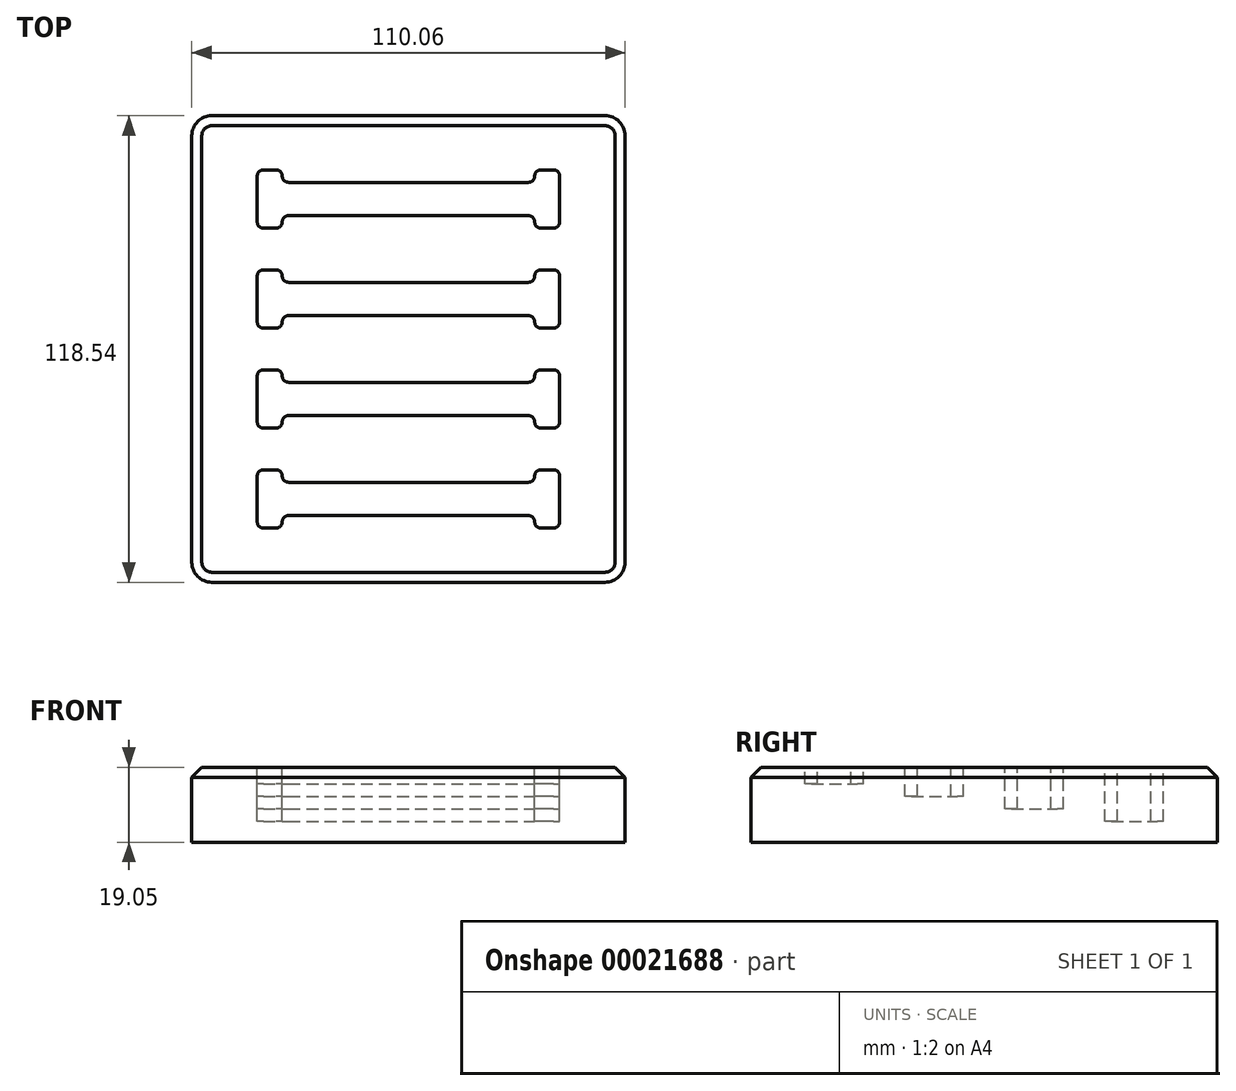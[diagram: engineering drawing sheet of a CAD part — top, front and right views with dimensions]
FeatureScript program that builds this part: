
annotation { "Feature Type Name" : "Feature", "Feature Type Description" : "" }
export const myFeature = defineFeature(function(context is Context, id is Id, definition is map)
    precondition{}
    {
        {
            var Q0;
            Q0=qCreatedBy(makeId("Top.planeOp"),FACE);
            var sketch = newSketch(context, id + "F0", { "sketchPlane" : qUnion([Q0])});
            skLineSegment(sketch, "E0.bottom", {"start": v(-55.03, 59.27) * mm, "end": v(55.03, 59.27) * mm});
            skLineSegment(sketch, "E0.top", {"start": v(-55.03, -59.27) * mm, "end": v(55.03, -59.27) * mm});
            skLineSegment(sketch, "E0.left", {"start": v(-55.03, 59.27) * mm, "end": v(-55.03, -59.27) * mm});
            skLineSegment(sketch, "E0.right", {"start": v(55.03, 59.27) * mm, "end": v(55.03, -59.27) * mm});
            skSolve(sketch);
        }
        {
            var Q0;
            Q0 = qSketchRegion(id + "F0", true);
            extrude(context, id + "F1", {"entities" : qUnion([Q0]), "depth" : 19.05 * mm});
        }
        {
            var Q0;
            Q0=makeQuery(id+"F1.opExtrude","CAP_FACE",FACE,{"disambiguationData":[OSD([sQuery(id+"F0.wireOp",EDGE,"E0.bottom"),sQuery(id+"F0.wireOp",EDGE,"E0.top"),sQuery(id+"F0.wireOp",EDGE,"E0.left"),sQuery(id+"F0.wireOp",EDGE,"E0.right")])],"isStart":false});
            var sketch = newSketch(context, id + "F2", { "sketchPlane" : qUnion([Q0])});
            skLineSegment(sketch, "E1.left", {"start": v(-38.42, 38.1) * mm, "end": v(-38.42, 33.87) * mm});
            skLineSegment(sketch, "E2", {"start": v(-38.42, 33.87) * mm, "end": v(-38.42, 30.7) * mm});
            skLineSegment(sketch, "E3", {"start": v(-38.42, 30.7) * mm, "end": v(-32.07, 30.7) * mm});
            skLineSegment(sketch, "E4", {"start": v(-32.07, 30.7) * mm, "end": v(-32.07, 33.87) * mm});
            skLineSegment(sketch, "E5", {"start": v(-32.07, 33.87) * mm, "end": v(0, 33.87) * mm});
            skLineSegment(sketch, "E6", {"start": v(-38.42, 38.1) * mm, "end": v(0, 38.1) * mm, "construction": true});
            skLineSegment(sketch, "E7.MirrorCS", {"start": v(-32.07, 42.33) * mm, "end": v(0, 42.33) * mm});
            skLineSegment(sketch, "E8.MirrorCS", {"start": v(-32.07, 45.5) * mm, "end": v(-32.07, 42.33) * mm});
            skLineSegment(sketch, "E9.MirrorCS", {"start": v(-38.42, 45.5) * mm, "end": v(-32.07, 45.5) * mm});
            skLineSegment(sketch, "E10.MirrorCS", {"start": v(-38.42, 38.1) * mm, "end": v(-38.42, 42.33) * mm});
            skLineSegment(sketch, "E11.MirrorCS", {"start": v(-38.42, 42.33) * mm, "end": v(-38.42, 45.5) * mm});
            skLineSegment(sketch, "E12", {"start": v(0, 33.87) * mm, "end": v(0, 42.33) * mm, "construction": true});
            skLineSegment(sketch, "E13.MirrorCS", {"start": v(32.07, 42.33) * mm, "end": v(0, 42.33) * mm});
            skLineSegment(sketch, "E14.MirrorCS", {"start": v(32.07, 45.5) * mm, "end": v(32.07, 42.33) * mm});
            skLineSegment(sketch, "E15.MirrorCS", {"start": v(38.42, 45.5) * mm, "end": v(32.07, 45.5) * mm});
            skLineSegment(sketch, "E16.MirrorCS", {"start": v(38.42, 42.33) * mm, "end": v(38.42, 45.5) * mm});
            skLineSegment(sketch, "E17.MirrorCS", {"start": v(38.42, 38.1) * mm, "end": v(38.42, 42.33) * mm});
            skLineSegment(sketch, "E18.MirrorCS", {"start": v(38.42, 38.1) * mm, "end": v(38.42, 33.87) * mm});
            skLineSegment(sketch, "E19.MirrorCS", {"start": v(38.42, 33.87) * mm, "end": v(38.42, 30.7) * mm});
            skLineSegment(sketch, "E20.MirrorCS", {"start": v(38.42, 30.7) * mm, "end": v(32.07, 30.7) * mm});
            skLineSegment(sketch, "E21.MirrorCS", {"start": v(32.07, 33.87) * mm, "end": v(0, 33.87) * mm});
            skLineSegment(sketch, "E22.MirrorCS", {"start": v(32.07, 30.7) * mm, "end": v(32.07, 33.87) * mm});
            skSolve(sketch);
        }
        {
            var Q0;
            Q0 = qSketchRegion(id + "F2", true);
            extrude(context, id + "F3", {"entities" : qUnion([Q0]), "operationType" : NewBodyOperationType.REMOVE, "oppositeDirection" : true, "depth" : 13.76 * mm});
        }
        {
            var Q0;
            Q0=makeQuery(id+"F1.opExtrude","CAP_FACE",FACE,{"disambiguationData":[OSD([sQuery(id+"F0.wireOp",EDGE,"E0.bottom"),sQuery(id+"F0.wireOp",EDGE,"E0.top"),sQuery(id+"F0.wireOp",EDGE,"E0.left"),sQuery(id+"F0.wireOp",EDGE,"E0.right")])],"isStart":false});
            var sketch = newSketch(context, id + "F4", { "sketchPlane" : qUnion([Q0])});
            skLineSegment(sketch, "E23.left", {"start": v(-38.42, 12.7) * mm, "end": v(-38.42, 8.47) * mm});
            skLineSegment(sketch, "E24", {"start": v(-38.42, 8.47) * mm, "end": v(-38.42, 5.3) * mm});
            skLineSegment(sketch, "E25", {"start": v(-38.42, 5.3) * mm, "end": v(-32.07, 5.3) * mm});
            skLineSegment(sketch, "E26", {"start": v(-32.07, 5.3) * mm, "end": v(-32.07, 8.47) * mm});
            skLineSegment(sketch, "E27", {"start": v(-32.07, 8.47) * mm, "end": v(0, 8.47) * mm});
            skLineSegment(sketch, "E28", {"start": v(-38.42, 12.7) * mm, "end": v(3.73, 12.7) * mm, "construction": true});
            skLineSegment(sketch, "E29.MirrorCS", {"start": v(-32.07, 16.93) * mm, "end": v(0, 16.93) * mm});
            skLineSegment(sketch, "E30.MirrorCS", {"start": v(-32.07, 20.1) * mm, "end": v(-32.07, 16.93) * mm});
            skLineSegment(sketch, "E31.MirrorCS", {"start": v(-38.42, 20.1) * mm, "end": v(-32.07, 20.1) * mm});
            skLineSegment(sketch, "E32.MirrorCS", {"start": v(-38.42, 12.7) * mm, "end": v(-38.42, 16.93) * mm});
            skLineSegment(sketch, "E33.MirrorCS", {"start": v(-38.42, 16.93) * mm, "end": v(-38.42, 20.1) * mm});
            skLineSegment(sketch, "E34", {"start": v(0, 8.47) * mm, "end": v(0, 16.93) * mm, "construction": true});
            skLineSegment(sketch, "E35.MirrorCS", {"start": v(32.07, 16.93) * mm, "end": v(0, 16.93) * mm});
            skLineSegment(sketch, "E36.MirrorCS", {"start": v(32.07, 20.1) * mm, "end": v(32.07, 16.93) * mm});
            skLineSegment(sketch, "E37.MirrorCS", {"start": v(38.42, 20.1) * mm, "end": v(32.07, 20.1) * mm});
            skLineSegment(sketch, "E38.MirrorCS", {"start": v(38.42, 16.93) * mm, "end": v(38.42, 20.1) * mm});
            skLineSegment(sketch, "E39.MirrorCS", {"start": v(38.42, 12.7) * mm, "end": v(38.42, 16.93) * mm});
            skLineSegment(sketch, "E40.MirrorCS", {"start": v(38.42, 12.7) * mm, "end": v(38.42, 8.47) * mm});
            skLineSegment(sketch, "E41.MirrorCS", {"start": v(38.42, 8.47) * mm, "end": v(38.42, 5.3) * mm});
            skLineSegment(sketch, "E42.MirrorCS", {"start": v(38.42, 5.3) * mm, "end": v(32.07, 5.3) * mm});
            skLineSegment(sketch, "E43.MirrorCS", {"start": v(32.07, 8.47) * mm, "end": v(0, 8.47) * mm});
            skLineSegment(sketch, "E44.MirrorCS", {"start": v(32.07, 5.3) * mm, "end": v(32.07, 8.47) * mm});
            skSolve(sketch);
        }
        {
            var Q0;
            Q0 = qSketchRegion(id + "F4", true);
            extrude(context, id + "F5", {"entities" : qUnion([Q0]), "operationType" : NewBodyOperationType.REMOVE, "oppositeDirection" : true, "depth" : 10.58 * mm});
        }
        {
            var Q0;
            Q0=makeQuery(id+"F1.opExtrude","CAP_FACE",FACE,{"disambiguationData":[OSD([sQuery(id+"F0.wireOp",EDGE,"E0.bottom"),sQuery(id+"F0.wireOp",EDGE,"E0.top"),sQuery(id+"F0.wireOp",EDGE,"E0.left"),sQuery(id+"F0.wireOp",EDGE,"E0.right")])],"isStart":false});
            var sketch = newSketch(context, id + "F6", { "sketchPlane" : qUnion([Q0])});
            skLineSegment(sketch, "E45.left", {"start": v(-38.42, -12.7) * mm, "end": v(-38.42, -16.93) * mm});
            skLineSegment(sketch, "E46", {"start": v(-38.42, -16.93) * mm, "end": v(-38.42, -20.1) * mm});
            skLineSegment(sketch, "E47", {"start": v(-38.42, -20.1) * mm, "end": v(-32.07, -20.1) * mm});
            skLineSegment(sketch, "E48", {"start": v(-32.07, -20.1) * mm, "end": v(-32.07, -16.93) * mm});
            skLineSegment(sketch, "E49", {"start": v(-32.07, -16.93) * mm, "end": v(0, -16.93) * mm});
            skLineSegment(sketch, "E50", {"start": v(-38.42, -12.7) * mm, "end": v(-19.4, -12.7) * mm, "construction": true});
            skLineSegment(sketch, "E51.MirrorCS", {"start": v(-32.07, -8.47) * mm, "end": v(0, -8.47) * mm});
            skLineSegment(sketch, "E52.MirrorCS", {"start": v(-32.07, -5.3) * mm, "end": v(-32.07, -8.47) * mm});
            skLineSegment(sketch, "E53.MirrorCS", {"start": v(-38.42, -5.3) * mm, "end": v(-32.07, -5.3) * mm});
            skLineSegment(sketch, "E54.MirrorCS", {"start": v(-38.42, -12.7) * mm, "end": v(-38.42, -8.47) * mm});
            skLineSegment(sketch, "E55.MirrorCS", {"start": v(-38.42, -8.47) * mm, "end": v(-38.42, -5.3) * mm});
            skLineSegment(sketch, "E56", {"start": v(0, -16.93) * mm, "end": v(0, -8.47) * mm, "construction": true});
            skLineSegment(sketch, "E57.MirrorCS", {"start": v(32.07, -8.47) * mm, "end": v(0, -8.47) * mm});
            skLineSegment(sketch, "E58.MirrorCS", {"start": v(32.07, -5.3) * mm, "end": v(32.07, -8.47) * mm});
            skLineSegment(sketch, "E59.MirrorCS", {"start": v(38.42, -5.3) * mm, "end": v(32.07, -5.3) * mm});
            skLineSegment(sketch, "E60.MirrorCS", {"start": v(38.42, -8.47) * mm, "end": v(38.42, -5.3) * mm});
            skLineSegment(sketch, "E61.MirrorCS", {"start": v(38.42, -12.7) * mm, "end": v(38.42, -8.47) * mm});
            skLineSegment(sketch, "E62.MirrorCS", {"start": v(38.42, -12.7) * mm, "end": v(38.42, -16.93) * mm});
            skLineSegment(sketch, "E63.MirrorCS", {"start": v(38.42, -16.93) * mm, "end": v(38.42, -20.1) * mm});
            skLineSegment(sketch, "E64.MirrorCS", {"start": v(38.42, -20.1) * mm, "end": v(32.07, -20.1) * mm});
            skLineSegment(sketch, "E65.MirrorCS", {"start": v(32.07, -16.93) * mm, "end": v(0, -16.93) * mm});
            skLineSegment(sketch, "E66.MirrorCS", {"start": v(32.07, -20.1) * mm, "end": v(32.07, -16.93) * mm});
            skSolve(sketch);
        }
        {
            var Q0;
            Q0 = qSketchRegion(id + "F6", true);
            extrude(context, id + "F7", {"entities" : qUnion([Q0]), "operationType" : NewBodyOperationType.REMOVE, "oppositeDirection" : true, "depth" : 7.4 * mm});
        }
        {
            var Q0;
            Q0=makeQuery(id+"F1.opExtrude","CAP_FACE",FACE,{"disambiguationData":[OSD([sQuery(id+"F0.wireOp",EDGE,"E0.bottom"),sQuery(id+"F0.wireOp",EDGE,"E0.top"),sQuery(id+"F0.wireOp",EDGE,"E0.left"),sQuery(id+"F0.wireOp",EDGE,"E0.right")])],"isStart":false});
            var sketch = newSketch(context, id + "F8", { "sketchPlane" : qUnion([Q0])});
            skLineSegment(sketch, "E67.left", {"start": v(-38.42, -38.1) * mm, "end": v(-38.42, -42.33) * mm});
            skLineSegment(sketch, "E68", {"start": v(-38.42, -42.33) * mm, "end": v(-38.42, -45.5) * mm});
            skLineSegment(sketch, "E69", {"start": v(-38.42, -45.5) * mm, "end": v(-32.07, -45.5) * mm});
            skLineSegment(sketch, "E70", {"start": v(-32.07, -45.5) * mm, "end": v(-32.07, -42.33) * mm});
            skLineSegment(sketch, "E71", {"start": v(-32.07, -42.33) * mm, "end": v(0, -42.33) * mm});
            skLineSegment(sketch, "E72", {"start": v(-38.42, -38.1) * mm, "end": v(-1.73, -38.1) * mm, "construction": true});
            skLineSegment(sketch, "E73.MirrorCS", {"start": v(-32.07, -33.87) * mm, "end": v(0, -33.87) * mm});
            skLineSegment(sketch, "E74.MirrorCS", {"start": v(-32.07, -30.7) * mm, "end": v(-32.07, -33.87) * mm});
            skLineSegment(sketch, "E75.MirrorCS", {"start": v(-38.42, -30.7) * mm, "end": v(-32.07, -30.7) * mm});
            skLineSegment(sketch, "E76.MirrorCS", {"start": v(-38.42, -38.1) * mm, "end": v(-38.42, -33.87) * mm});
            skLineSegment(sketch, "E77.MirrorCS", {"start": v(-38.42, -33.87) * mm, "end": v(-38.42, -30.7) * mm});
            skLineSegment(sketch, "E78", {"start": v(0, -42.33) * mm, "end": v(0, -33.87) * mm, "construction": true});
            skLineSegment(sketch, "E79.MirrorCS", {"start": v(32.07, -33.87) * mm, "end": v(0, -33.87) * mm});
            skLineSegment(sketch, "E80.MirrorCS", {"start": v(32.07, -30.7) * mm, "end": v(32.07, -33.87) * mm});
            skLineSegment(sketch, "E81.MirrorCS", {"start": v(38.42, -30.7) * mm, "end": v(32.07, -30.7) * mm});
            skLineSegment(sketch, "E82.MirrorCS", {"start": v(38.42, -33.87) * mm, "end": v(38.42, -30.7) * mm});
            skLineSegment(sketch, "E83.MirrorCS", {"start": v(38.42, -38.1) * mm, "end": v(38.42, -33.87) * mm});
            skLineSegment(sketch, "E84.MirrorCS", {"start": v(38.42, -38.1) * mm, "end": v(38.42, -42.33) * mm});
            skLineSegment(sketch, "E85.MirrorCS", {"start": v(38.42, -42.33) * mm, "end": v(38.42, -45.5) * mm});
            skLineSegment(sketch, "E86.MirrorCS", {"start": v(38.42, -45.5) * mm, "end": v(32.07, -45.5) * mm});
            skLineSegment(sketch, "E87.MirrorCS", {"start": v(32.07, -42.33) * mm, "end": v(0, -42.33) * mm});
            skLineSegment(sketch, "E88.MirrorCS", {"start": v(32.07, -45.5) * mm, "end": v(32.07, -42.33) * mm});
            skSolve(sketch);
        }
        {
            var Q0;
            Q0 = qSketchRegion(id + "F8", true);
            extrude(context, id + "F9", {"entities" : qUnion([Q0]), "operationType" : NewBodyOperationType.REMOVE, "oppositeDirection" : true, "depth" : 4.23 * mm});
        }
        {
            var Q0;
            Q0=makeQuery(id+"F9.boolean.opBoolean","COPY",EDGE,{"derivedFrom":makeQuery(id+"F9.opExtrude","SWEPT_EDGE",EDGE,{"disambiguationData":[OSD([sQuery(id+"F8.wireOp",EDGE,"E75.MirrorCS"),sQuery(id+"F8.wireOp",EDGE,"E77.MirrorCS")])]})});
            var Q1;
            Q1=makeQuery(id+"F7.boolean.opBoolean","COPY",EDGE,{"derivedFrom":makeQuery(id+"F7.opExtrude","SWEPT_EDGE",EDGE,{"disambiguationData":[OSD([sQuery(id+"F6.wireOp",EDGE,"E53.MirrorCS"),sQuery(id+"F6.wireOp",EDGE,"E55.MirrorCS")])]})});
            var Q2;
            Q2=makeQuery(id+"F5.boolean.opBoolean","COPY",EDGE,{"derivedFrom":makeQuery(id+"F5.opExtrude","SWEPT_EDGE",EDGE,{"disambiguationData":[OSD([sQuery(id+"F4.wireOp",EDGE,"E31.MirrorCS"),sQuery(id+"F4.wireOp",EDGE,"E33.MirrorCS")])]})});
            var Q3;
            Q3=makeQuery(id+"F3.boolean.opBoolean","COPY",EDGE,{"derivedFrom":makeQuery(id+"F3.opExtrude","SWEPT_EDGE",EDGE,{"disambiguationData":[OSD([sQuery(id+"F2.wireOp",EDGE,"E9.MirrorCS"),sQuery(id+"F2.wireOp",EDGE,"E11.MirrorCS")])]})});
            var Q4;
            Q4=makeQuery(id+"F3.boolean.opBoolean","COPY",EDGE,{"derivedFrom":makeQuery(id+"F3.opExtrude","SWEPT_EDGE",EDGE,{"disambiguationData":[OSD([sQuery(id+"F2.wireOp",EDGE,"E7.MirrorCS"),sQuery(id+"F2.wireOp",EDGE,"E8.MirrorCS")])]})});
            var Q5;
            Q5=makeQuery(id+"F5.boolean.opBoolean","COPY",EDGE,{"derivedFrom":makeQuery(id+"F5.opExtrude","SWEPT_EDGE",EDGE,{"disambiguationData":[OSD([sQuery(id+"F4.wireOp",EDGE,"E29.MirrorCS"),sQuery(id+"F4.wireOp",EDGE,"E30.MirrorCS")])]})});
            var Q6;
            Q6=makeQuery(id+"F7.boolean.opBoolean","COPY",EDGE,{"derivedFrom":makeQuery(id+"F7.opExtrude","SWEPT_EDGE",EDGE,{"disambiguationData":[OSD([sQuery(id+"F6.wireOp",EDGE,"E51.MirrorCS"),sQuery(id+"F6.wireOp",EDGE,"E52.MirrorCS")])]})});
            var Q7;
            Q7=makeQuery(id+"F9.boolean.opBoolean","COPY",EDGE,{"derivedFrom":makeQuery(id+"F9.opExtrude","SWEPT_EDGE",EDGE,{"disambiguationData":[OSD([sQuery(id+"F8.wireOp",EDGE,"E73.MirrorCS"),sQuery(id+"F8.wireOp",EDGE,"E74.MirrorCS")])]})});
            var Q8;
            Q8=makeQuery(id+"F9.boolean.opBoolean","COPY",EDGE,{"derivedFrom":makeQuery(id+"F9.opExtrude","SWEPT_EDGE",EDGE,{"disambiguationData":[OSD([sQuery(id+"F8.wireOp",EDGE,"E68"),sQuery(id+"F8.wireOp",EDGE,"E69")])]})});
            var Q9;
            Q9=makeQuery(id+"F9.boolean.opBoolean","COPY",EDGE,{"derivedFrom":makeQuery(id+"F9.opExtrude","SWEPT_EDGE",EDGE,{"disambiguationData":[OSD([sQuery(id+"F8.wireOp",EDGE,"E70"),sQuery(id+"F8.wireOp",EDGE,"E71")])]})});
            var Q10;
            Q10=makeQuery(id+"F7.boolean.opBoolean","COPY",EDGE,{"derivedFrom":makeQuery(id+"F7.opExtrude","SWEPT_EDGE",EDGE,{"disambiguationData":[OSD([sQuery(id+"F6.wireOp",EDGE,"E46"),sQuery(id+"F6.wireOp",EDGE,"E47")])]})});
            var Q11;
            Q11=makeQuery(id+"F7.boolean.opBoolean","COPY",EDGE,{"derivedFrom":makeQuery(id+"F7.opExtrude","SWEPT_EDGE",EDGE,{"disambiguationData":[OSD([sQuery(id+"F6.wireOp",EDGE,"E48"),sQuery(id+"F6.wireOp",EDGE,"E49")])]})});
            var Q12;
            Q12=makeQuery(id+"F5.boolean.opBoolean","COPY",EDGE,{"derivedFrom":makeQuery(id+"F5.opExtrude","SWEPT_EDGE",EDGE,{"disambiguationData":[OSD([sQuery(id+"F4.wireOp",EDGE,"E26"),sQuery(id+"F4.wireOp",EDGE,"E27")])]})});
            var Q13;
            Q13=makeQuery(id+"F5.boolean.opBoolean","COPY",EDGE,{"derivedFrom":makeQuery(id+"F5.opExtrude","SWEPT_EDGE",EDGE,{"disambiguationData":[OSD([sQuery(id+"F4.wireOp",EDGE,"E24"),sQuery(id+"F4.wireOp",EDGE,"E25")])]})});
            var Q14;
            Q14=makeQuery(id+"F3.boolean.opBoolean","COPY",EDGE,{"derivedFrom":makeQuery(id+"F3.opExtrude","SWEPT_EDGE",EDGE,{"disambiguationData":[OSD([sQuery(id+"F2.wireOp",EDGE,"E4"),sQuery(id+"F2.wireOp",EDGE,"E5")])]})});
            var Q15;
            Q15=makeQuery(id+"F3.boolean.opBoolean","COPY",EDGE,{"derivedFrom":makeQuery(id+"F3.opExtrude","SWEPT_EDGE",EDGE,{"disambiguationData":[OSD([sQuery(id+"F2.wireOp",EDGE,"E2"),sQuery(id+"F2.wireOp",EDGE,"E3")])]})});
            var Q16;
            Q16=makeQuery(id+"F9.boolean.opBoolean","COPY",EDGE,{"derivedFrom":makeQuery(id+"F9.opExtrude","SWEPT_EDGE",EDGE,{"disambiguationData":[OSD([sQuery(id+"F8.wireOp",EDGE,"E86.MirrorCS"),sQuery(id+"F8.wireOp",EDGE,"E88.MirrorCS")])]})});
            var Q17;
            Q17=makeQuery(id+"F9.boolean.opBoolean","COPY",EDGE,{"derivedFrom":makeQuery(id+"F9.opExtrude","SWEPT_EDGE",EDGE,{"disambiguationData":[OSD([sQuery(id+"F8.wireOp",EDGE,"E87.MirrorCS"),sQuery(id+"F8.wireOp",EDGE,"E88.MirrorCS")])]})});
            var Q18;
            Q18=makeQuery(id+"F9.boolean.opBoolean","COPY",EDGE,{"derivedFrom":makeQuery(id+"F9.opExtrude","SWEPT_EDGE",EDGE,{"disambiguationData":[OSD([sQuery(id+"F8.wireOp",EDGE,"E79.MirrorCS"),sQuery(id+"F8.wireOp",EDGE,"E80.MirrorCS")])]})});
            var Q19;
            Q19=makeQuery(id+"F7.boolean.opBoolean","COPY",EDGE,{"derivedFrom":makeQuery(id+"F7.opExtrude","SWEPT_EDGE",EDGE,{"disambiguationData":[OSD([sQuery(id+"F6.wireOp",EDGE,"E64.MirrorCS"),sQuery(id+"F6.wireOp",EDGE,"E66.MirrorCS")])]})});
            var Q20;
            Q20=makeQuery(id+"F7.boolean.opBoolean","COPY",EDGE,{"derivedFrom":makeQuery(id+"F7.opExtrude","SWEPT_EDGE",EDGE,{"disambiguationData":[OSD([sQuery(id+"F6.wireOp",EDGE,"E65.MirrorCS"),sQuery(id+"F6.wireOp",EDGE,"E66.MirrorCS")])]})});
            var Q21;
            Q21=makeQuery(id+"F7.boolean.opBoolean","COPY",EDGE,{"derivedFrom":makeQuery(id+"F7.opExtrude","SWEPT_EDGE",EDGE,{"disambiguationData":[OSD([sQuery(id+"F6.wireOp",EDGE,"E57.MirrorCS"),sQuery(id+"F6.wireOp",EDGE,"E58.MirrorCS")])]})});
            var Q22;
            Q22=makeQuery(id+"F5.boolean.opBoolean","COPY",EDGE,{"derivedFrom":makeQuery(id+"F5.opExtrude","SWEPT_EDGE",EDGE,{"disambiguationData":[OSD([sQuery(id+"F4.wireOp",EDGE,"E42.MirrorCS"),sQuery(id+"F4.wireOp",EDGE,"E44.MirrorCS")])]})});
            var Q23;
            Q23=makeQuery(id+"F5.boolean.opBoolean","COPY",EDGE,{"derivedFrom":makeQuery(id+"F5.opExtrude","SWEPT_EDGE",EDGE,{"disambiguationData":[OSD([sQuery(id+"F4.wireOp",EDGE,"E43.MirrorCS"),sQuery(id+"F4.wireOp",EDGE,"E44.MirrorCS")])]})});
            var Q24;
            Q24=makeQuery(id+"F5.boolean.opBoolean","COPY",EDGE,{"derivedFrom":makeQuery(id+"F5.opExtrude","SWEPT_EDGE",EDGE,{"disambiguationData":[OSD([sQuery(id+"F4.wireOp",EDGE,"E35.MirrorCS"),sQuery(id+"F4.wireOp",EDGE,"E36.MirrorCS")])]})});
            var Q25;
            Q25=makeQuery(id+"F3.boolean.opBoolean","COPY",EDGE,{"derivedFrom":makeQuery(id+"F3.opExtrude","SWEPT_EDGE",EDGE,{"disambiguationData":[OSD([sQuery(id+"F2.wireOp",EDGE,"E20.MirrorCS"),sQuery(id+"F2.wireOp",EDGE,"E22.MirrorCS")])]})});
            var Q26;
            Q26=makeQuery(id+"F3.boolean.opBoolean","COPY",EDGE,{"derivedFrom":makeQuery(id+"F3.opExtrude","SWEPT_EDGE",EDGE,{"disambiguationData":[OSD([sQuery(id+"F2.wireOp",EDGE,"E21.MirrorCS"),sQuery(id+"F2.wireOp",EDGE,"E22.MirrorCS")])]})});
            var Q27;
            Q27=makeQuery(id+"F3.boolean.opBoolean","COPY",EDGE,{"derivedFrom":makeQuery(id+"F3.opExtrude","SWEPT_EDGE",EDGE,{"disambiguationData":[OSD([sQuery(id+"F2.wireOp",EDGE,"E13.MirrorCS"),sQuery(id+"F2.wireOp",EDGE,"E14.MirrorCS")])]})});
            var Q28;
            Q28=makeQuery(id+"F3.boolean.opBoolean","COPY",EDGE,{"derivedFrom":makeQuery(id+"F3.opExtrude","SWEPT_EDGE",EDGE,{"disambiguationData":[OSD([sQuery(id+"F2.wireOp",EDGE,"E19.MirrorCS"),sQuery(id+"F2.wireOp",EDGE,"E20.MirrorCS")])]})});
            var Q29;
            Q29=makeQuery(id+"F5.boolean.opBoolean","COPY",EDGE,{"derivedFrom":makeQuery(id+"F5.opExtrude","SWEPT_EDGE",EDGE,{"disambiguationData":[OSD([sQuery(id+"F4.wireOp",EDGE,"E41.MirrorCS"),sQuery(id+"F4.wireOp",EDGE,"E42.MirrorCS")])]})});
            var Q30;
            Q30=makeQuery(id+"F7.boolean.opBoolean","COPY",EDGE,{"derivedFrom":makeQuery(id+"F7.opExtrude","SWEPT_EDGE",EDGE,{"disambiguationData":[OSD([sQuery(id+"F6.wireOp",EDGE,"E63.MirrorCS"),sQuery(id+"F6.wireOp",EDGE,"E64.MirrorCS")])]})});
            var Q31;
            Q31=makeQuery(id+"F9.boolean.opBoolean","COPY",EDGE,{"derivedFrom":makeQuery(id+"F9.opExtrude","SWEPT_EDGE",EDGE,{"disambiguationData":[OSD([sQuery(id+"F8.wireOp",EDGE,"E85.MirrorCS"),sQuery(id+"F8.wireOp",EDGE,"E86.MirrorCS")])]})});
            var Q32;
            Q32=makeQuery(id+"F3.boolean.opBoolean","COPY",EDGE,{"derivedFrom":makeQuery(id+"F3.opExtrude","SWEPT_EDGE",EDGE,{"disambiguationData":[OSD([sQuery(id+"F2.wireOp",EDGE,"E15.MirrorCS"),sQuery(id+"F2.wireOp",EDGE,"E16.MirrorCS")])]})});
            var Q33;
            Q33=makeQuery(id+"F5.boolean.opBoolean","COPY",EDGE,{"derivedFrom":makeQuery(id+"F5.opExtrude","SWEPT_EDGE",EDGE,{"disambiguationData":[OSD([sQuery(id+"F4.wireOp",EDGE,"E37.MirrorCS"),sQuery(id+"F4.wireOp",EDGE,"E38.MirrorCS")])]})});
            var Q34;
            Q34=makeQuery(id+"F7.boolean.opBoolean","COPY",EDGE,{"derivedFrom":makeQuery(id+"F7.opExtrude","SWEPT_EDGE",EDGE,{"disambiguationData":[OSD([sQuery(id+"F6.wireOp",EDGE,"E59.MirrorCS"),sQuery(id+"F6.wireOp",EDGE,"E60.MirrorCS")])]})});
            var Q35;
            Q35=makeQuery(id+"F9.boolean.opBoolean","COPY",EDGE,{"derivedFrom":makeQuery(id+"F9.opExtrude","SWEPT_EDGE",EDGE,{"disambiguationData":[OSD([sQuery(id+"F8.wireOp",EDGE,"E81.MirrorCS"),sQuery(id+"F8.wireOp",EDGE,"E82.MirrorCS")])]})});
            var Q36;
            Q36=makeQuery(id+"F3.boolean.opBoolean","COPY",EDGE,{"derivedFrom":makeQuery(id+"F3.opExtrude","SWEPT_EDGE",EDGE,{"disambiguationData":[OSD([sQuery(id+"F2.wireOp",EDGE,"E8.MirrorCS"),sQuery(id+"F2.wireOp",EDGE,"E9.MirrorCS")])]})});
            var Q37;
            Q37=makeQuery(id+"F5.boolean.opBoolean","COPY",EDGE,{"derivedFrom":makeQuery(id+"F5.opExtrude","SWEPT_EDGE",EDGE,{"disambiguationData":[OSD([sQuery(id+"F4.wireOp",EDGE,"E30.MirrorCS"),sQuery(id+"F4.wireOp",EDGE,"E31.MirrorCS")])]})});
            var Q38;
            Q38=makeQuery(id+"F7.boolean.opBoolean","COPY",EDGE,{"derivedFrom":makeQuery(id+"F7.opExtrude","SWEPT_EDGE",EDGE,{"disambiguationData":[OSD([sQuery(id+"F6.wireOp",EDGE,"E52.MirrorCS"),sQuery(id+"F6.wireOp",EDGE,"E53.MirrorCS")])]})});
            var Q39;
            Q39=makeQuery(id+"F9.boolean.opBoolean","COPY",EDGE,{"derivedFrom":makeQuery(id+"F9.opExtrude","SWEPT_EDGE",EDGE,{"disambiguationData":[OSD([sQuery(id+"F8.wireOp",EDGE,"E74.MirrorCS"),sQuery(id+"F8.wireOp",EDGE,"E75.MirrorCS")])]})});
            var Q40;
            Q40=makeQuery(id+"F9.boolean.opBoolean","COPY",EDGE,{"derivedFrom":makeQuery(id+"F9.opExtrude","SWEPT_EDGE",EDGE,{"disambiguationData":[OSD([sQuery(id+"F8.wireOp",EDGE,"E69"),sQuery(id+"F8.wireOp",EDGE,"E70")])]})});
            var Q41;
            Q41=makeQuery(id+"F7.boolean.opBoolean","COPY",EDGE,{"derivedFrom":makeQuery(id+"F7.opExtrude","SWEPT_EDGE",EDGE,{"disambiguationData":[OSD([sQuery(id+"F6.wireOp",EDGE,"E47"),sQuery(id+"F6.wireOp",EDGE,"E48")])]})});
            var Q42;
            Q42=makeQuery(id+"F5.boolean.opBoolean","COPY",EDGE,{"derivedFrom":makeQuery(id+"F5.opExtrude","SWEPT_EDGE",EDGE,{"disambiguationData":[OSD([sQuery(id+"F4.wireOp",EDGE,"E25"),sQuery(id+"F4.wireOp",EDGE,"E26")])]})});
            var Q43;
            Q43=makeQuery(id+"F3.boolean.opBoolean","COPY",EDGE,{"derivedFrom":makeQuery(id+"F3.opExtrude","SWEPT_EDGE",EDGE,{"disambiguationData":[OSD([sQuery(id+"F2.wireOp",EDGE,"E3"),sQuery(id+"F2.wireOp",EDGE,"E4")])]})});
            var Q44;
            Q44=makeQuery(id+"F9.boolean.opBoolean","COPY",EDGE,{"derivedFrom":makeQuery(id+"F9.opExtrude","SWEPT_EDGE",EDGE,{"disambiguationData":[OSD([sQuery(id+"F8.wireOp",EDGE,"E80.MirrorCS"),sQuery(id+"F8.wireOp",EDGE,"E81.MirrorCS")])]})});
            var Q45;
            Q45=makeQuery(id+"F7.boolean.opBoolean","COPY",EDGE,{"derivedFrom":makeQuery(id+"F7.opExtrude","SWEPT_EDGE",EDGE,{"disambiguationData":[OSD([sQuery(id+"F6.wireOp",EDGE,"E58.MirrorCS"),sQuery(id+"F6.wireOp",EDGE,"E59.MirrorCS")])]})});
            var Q46;
            Q46=makeQuery(id+"F5.boolean.opBoolean","COPY",EDGE,{"derivedFrom":makeQuery(id+"F5.opExtrude","SWEPT_EDGE",EDGE,{"disambiguationData":[OSD([sQuery(id+"F4.wireOp",EDGE,"E36.MirrorCS"),sQuery(id+"F4.wireOp",EDGE,"E37.MirrorCS")])]})});
            var Q47;
            Q47=makeQuery(id+"F3.boolean.opBoolean","COPY",EDGE,{"derivedFrom":makeQuery(id+"F3.opExtrude","SWEPT_EDGE",EDGE,{"disambiguationData":[OSD([sQuery(id+"F2.wireOp",EDGE,"E14.MirrorCS"),sQuery(id+"F2.wireOp",EDGE,"E15.MirrorCS")])]})});
            fillet(context, id + "F10", {"entities" : qUnion([Q0, Q1, Q2, Q3, Q4, Q5, Q6, Q7, Q8, Q9, Q10, Q11, Q12, Q13, Q14, Q15, Q16, Q17, Q18, Q19, Q20, Q21, Q22, Q23, Q24, Q25, Q26, Q27, Q28, Q29, Q30, Q31, Q32, Q33, Q34, Q35, Q36, Q37, Q38, Q39, Q40, Q41, Q42, Q43, Q44, Q45, Q46, Q47]), "radius" : 1.59 * mm, "tangentPropagation" : true, "allowEdgeOverflow" : false});
        }
        {
            var Q0;
            Q0=makeQuery(id+"F1.opExtrude","SWEPT_EDGE",EDGE,{"disambiguationData":[OSD([sQuery(id+"F0.wireOp",EDGE,"E0.top"),sQuery(id+"F0.wireOp",EDGE,"E0.left")])]});
            var Q1;
            Q1=makeQuery(id+"F1.opExtrude","SWEPT_EDGE",EDGE,{"disambiguationData":[OSD([sQuery(id+"F0.wireOp",EDGE,"E0.top"),sQuery(id+"F0.wireOp",EDGE,"E0.right")])]});
            var Q2;
            Q2=makeQuery(id+"F1.opExtrude","SWEPT_EDGE",EDGE,{"disambiguationData":[OSD([sQuery(id+"F0.wireOp",EDGE,"E0.bottom"),sQuery(id+"F0.wireOp",EDGE,"E0.right")])]});
            var Q3;
            Q3=makeQuery(id+"F1.opExtrude","SWEPT_EDGE",EDGE,{"disambiguationData":[OSD([sQuery(id+"F0.wireOp",EDGE,"E0.bottom"),sQuery(id+"F0.wireOp",EDGE,"E0.left")])]});
            fillet(context, id + "F11", {"entities" : qUnion([Q0, Q1, Q2, Q3]), "radius" : 5.08 * mm, "tangentPropagation" : true, "allowEdgeOverflow" : false});
        }
        {
            var Q0;
            Q0=makeQuery(id+"F1.opExtrude","CAP_EDGE",EDGE,{"disambiguationData":[OSD([sQuery(id+"F0.wireOp",EDGE,"E0.right")])],"isStart":false});
            var Q1;
            {var subQ0=sQuery(id+"F0.wireOp",EDGE,"E0.top");var subQ1=sQuery(id+"F0.wireOp",EDGE,"E0.right");Q1=makeQuery(id+"F11.opFillet","BLEND_EDGE",EDGE,{"blendedFrom":[makeQuery(id+"F1.opExtrude","SWEPT_EDGE",EDGE,{"disambiguationData":[OSD([subQ0,subQ1])]}),makeQuery(id+"F1.opExtrude","CAP_FACE",FACE,{"disambiguationData":[OSD([sQuery(id+"F0.wireOp",EDGE,"E0.bottom"),subQ0,sQuery(id+"F0.wireOp",EDGE,"E0.left"),subQ1])],"isStart":false})],"blendedInto":[makeQuery(id+"F1.opExtrude","CAP_FACE",FACE,{"disambiguationData":[OSD([sQuery(id+"F0.wireOp",EDGE,"E0.bottom"),subQ0,sQuery(id+"F0.wireOp",EDGE,"E0.left"),subQ1])],"isStart":false})]});}
            var Q2;
            Q2=makeQuery(id+"F1.opExtrude","CAP_EDGE",EDGE,{"disambiguationData":[OSD([sQuery(id+"F0.wireOp",EDGE,"E0.top")])],"isStart":false});
            var Q3;
            {var subQ0=sQuery(id+"F0.wireOp",EDGE,"E0.top");var subQ1=sQuery(id+"F0.wireOp",EDGE,"E0.left");Q3=makeQuery(id+"F11.opFillet","BLEND_EDGE",EDGE,{"blendedFrom":[makeQuery(id+"F1.opExtrude","SWEPT_EDGE",EDGE,{"disambiguationData":[OSD([subQ0,subQ1])]}),makeQuery(id+"F1.opExtrude","CAP_FACE",FACE,{"disambiguationData":[OSD([sQuery(id+"F0.wireOp",EDGE,"E0.bottom"),subQ0,subQ1,sQuery(id+"F0.wireOp",EDGE,"E0.right")])],"isStart":false})],"blendedInto":[makeQuery(id+"F1.opExtrude","CAP_FACE",FACE,{"disambiguationData":[OSD([sQuery(id+"F0.wireOp",EDGE,"E0.bottom"),subQ0,subQ1,sQuery(id+"F0.wireOp",EDGE,"E0.right")])],"isStart":false})]});}
            var Q4;
            Q4=makeQuery(id+"F1.opExtrude","CAP_EDGE",EDGE,{"disambiguationData":[OSD([sQuery(id+"F0.wireOp",EDGE,"E0.left")])],"isStart":false});
            var Q5;
            {var subQ0=sQuery(id+"F0.wireOp",EDGE,"E0.bottom");var subQ1=sQuery(id+"F0.wireOp",EDGE,"E0.left");Q5=makeQuery(id+"F11.opFillet","BLEND_EDGE",EDGE,{"blendedFrom":[makeQuery(id+"F1.opExtrude","SWEPT_EDGE",EDGE,{"disambiguationData":[OSD([subQ0,subQ1])]}),makeQuery(id+"F1.opExtrude","CAP_FACE",FACE,{"disambiguationData":[OSD([subQ0,sQuery(id+"F0.wireOp",EDGE,"E0.top"),subQ1,sQuery(id+"F0.wireOp",EDGE,"E0.right")])],"isStart":false})],"blendedInto":[makeQuery(id+"F1.opExtrude","CAP_FACE",FACE,{"disambiguationData":[OSD([subQ0,sQuery(id+"F0.wireOp",EDGE,"E0.top"),subQ1,sQuery(id+"F0.wireOp",EDGE,"E0.right")])],"isStart":false})]});}
            var Q6;
            Q6=makeQuery(id+"F1.opExtrude","CAP_EDGE",EDGE,{"disambiguationData":[OSD([sQuery(id+"F0.wireOp",EDGE,"E0.bottom")])],"isStart":false});
            var Q7;
            {var subQ0=sQuery(id+"F0.wireOp",EDGE,"E0.bottom");var subQ1=sQuery(id+"F0.wireOp",EDGE,"E0.right");Q7=makeQuery(id+"F11.opFillet","BLEND_EDGE",EDGE,{"blendedFrom":[makeQuery(id+"F1.opExtrude","SWEPT_EDGE",EDGE,{"disambiguationData":[OSD([subQ0,subQ1])]}),makeQuery(id+"F1.opExtrude","CAP_FACE",FACE,{"disambiguationData":[OSD([subQ0,sQuery(id+"F0.wireOp",EDGE,"E0.top"),sQuery(id+"F0.wireOp",EDGE,"E0.left"),subQ1])],"isStart":false})],"blendedInto":[makeQuery(id+"F1.opExtrude","CAP_FACE",FACE,{"disambiguationData":[OSD([subQ0,sQuery(id+"F0.wireOp",EDGE,"E0.top"),sQuery(id+"F0.wireOp",EDGE,"E0.left"),subQ1])],"isStart":false})]});}
            chamfer(context, id + "F12", {"entities" : qUnion([Q0, Q1, Q2, Q3, Q4, Q5, Q6, Q7]), "width" : 2.54 * mm, "tangentPropagation" : true});
        }
    });
